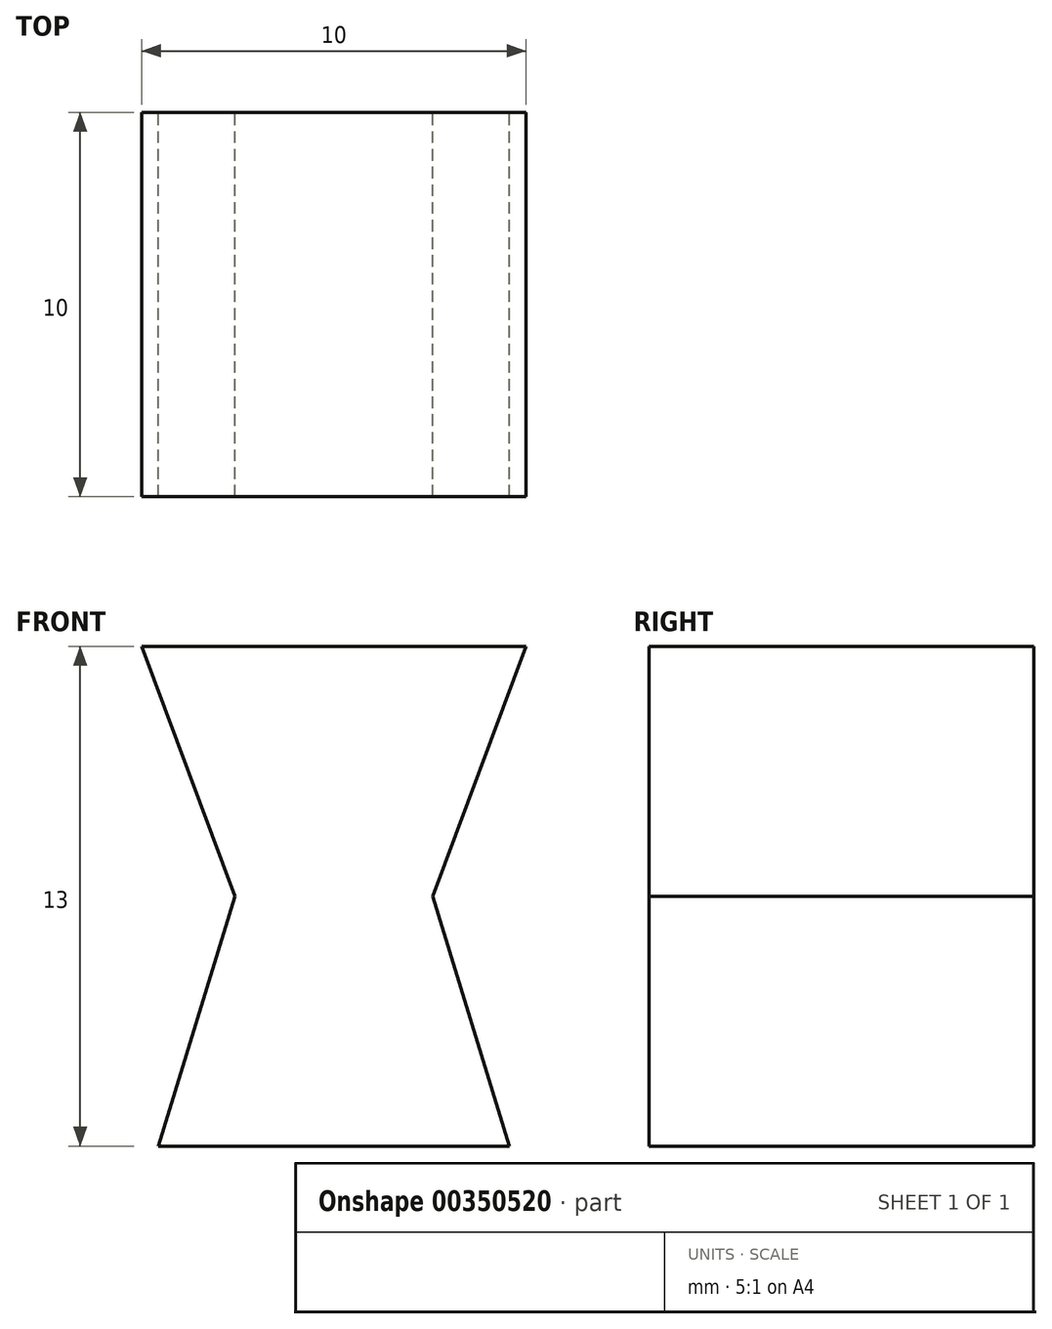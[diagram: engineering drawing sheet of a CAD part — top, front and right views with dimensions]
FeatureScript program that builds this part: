
annotation { "Feature Type Name" : "Feature", "Feature Type Description" : "" }
export const myFeature = defineFeature(function(context is Context, id is Id, definition is map)
    precondition{}
    {
        {
            var Q0;
            Q0=qCreatedBy(makeId("Front.planeOp"),FACE);
            var sketch = newSketch(context, id + "F0", { "sketchPlane" : qUnion([Q0])});
            skLineSegment(sketch, "E0.bottom", {"start": v(0, 0) * mm, "end": v(-6.67, 0) * mm, "construction": true});
            skLineSegment(sketch, "E0.top", {"start": v(0, 13) * mm, "end": v(-6.67, 13) * mm, "construction": true});
            skLineSegment(sketch, "E0.left", {"start": v(0, 0) * mm, "end": v(0, 13) * mm, "construction": true});
            skLineSegment(sketch, "E0.right", {"start": v(-6.67, 0) * mm, "end": v(-6.67, 13) * mm, "construction": true});
            skLineSegment(sketch, "E1", {"start": v(0, 13) * mm, "end": v(-5, 13) * mm});
            skLineSegment(sketch, "E2", {"start": v(0, 13) * mm, "end": v(0, 0) * mm, "construction": true});
            skLineSegment(sketch, "E3", {"start": v(0, 6.5) * mm, "end": v(-6.67, 6.5) * mm, "construction": true});
            skLineSegment(sketch, "E4", {"start": v(-5, 13) * mm, "end": v(-2.57, 6.5) * mm});
            skLineSegment(sketch, "E5", {"start": v(-2.57, 6.5) * mm, "end": v(-4.57, 0) * mm});
            skLineSegment(sketch, "E6", {"start": v(-4.57, 0) * mm, "end": v(0, 0) * mm});
            skLineSegment(sketch, "E7.MirrorCS", {"start": v(0, 13) * mm, "end": v(5, 13) * mm});
            skLineSegment(sketch, "E8.MirrorCS", {"start": v(5, 13) * mm, "end": v(2.57, 6.5) * mm});
            skLineSegment(sketch, "E9.MirrorCS", {"start": v(2.57, 6.5) * mm, "end": v(4.57, 0) * mm});
            skLineSegment(sketch, "E10.MirrorCS", {"start": v(4.57, 0) * mm, "end": v(0, 0) * mm});
            skSolve(sketch);
        }
        {
            var Q0;
            Q0=makeQuery(id+"F0.imprint","IMPRINT",FACE,{"disambiguationData":[TD([[makeQuery(id+"F0.imprint","IMPRINT",EDGE,{"derivedFrom":sQuery(id+"F0.wireOp",EDGE,"E1")}),1.0]])]});
            extrude(context, id + "F1", {"entities" : qUnion([Q0]), "depth" : 10 * mm, "offsetDistance" : 25 * mm});
        }
    });
